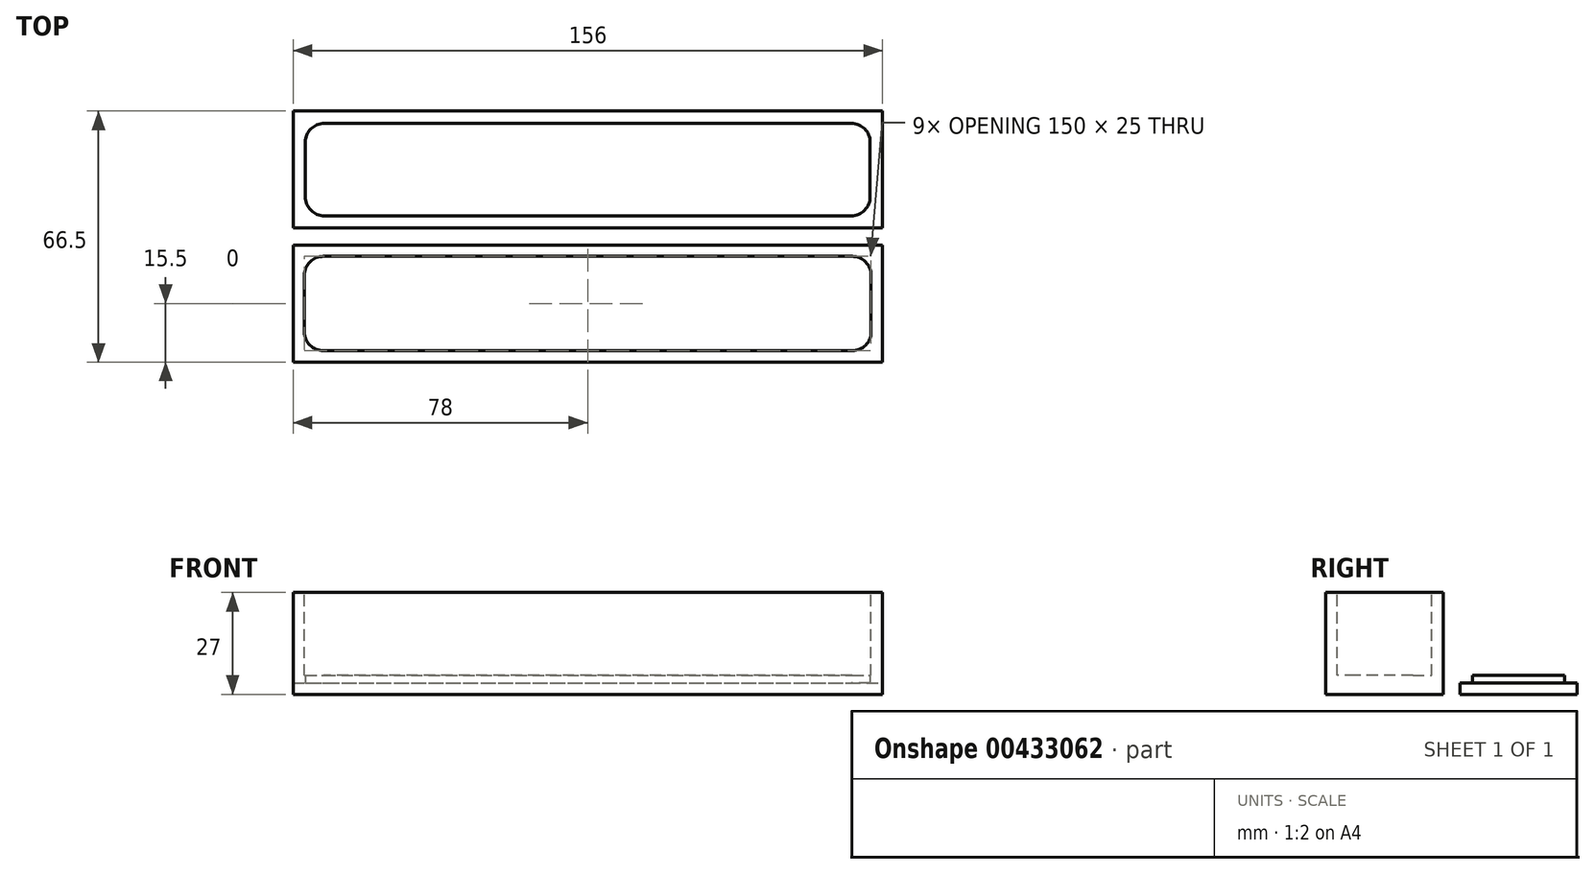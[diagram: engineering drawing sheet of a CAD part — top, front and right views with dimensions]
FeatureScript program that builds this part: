
annotation { "Feature Type Name" : "Feature", "Feature Type Description" : "" }
export const myFeature = defineFeature(function(context is Context, id is Id, definition is map)
    precondition{}
    {
        {
            var Q0;
            Q0=qCreatedBy(makeId("Top.planeOp"),FACE);
            var sketch = newSketch(context, id + "F0", { "sketchPlane" : qUnion([Q0])});
            skLineSegment(sketch, "E0.bottom", {"start": v(78, -15.5) * mm, "end": v(-78, -15.5) * mm});
            skLineSegment(sketch, "E0.top", {"start": v(78, 15.5) * mm, "end": v(-78, 15.5) * mm});
            skLineSegment(sketch, "E0.left", {"start": v(78, -15.5) * mm, "end": v(78, 15.5) * mm});
            skLineSegment(sketch, "E0.right", {"start": v(-78, -15.5) * mm, "end": v(-78, 15.5) * mm});
            skPoint(sketch, "E0.middle", {"position": v(0, 0) * mm});
            skSolve(sketch);
        }
        {
            var Q0;
            Q0 = qSketchRegion(id + "F0", true);
            extrude(context, id + "F1", {"entities" : qUnion([Q0]), "depth" : 27 * mm});
        }
        {
            var Q0;
            Q0=makeQuery(id+"F1.opExtrude","CAP_FACE",FACE,{"disambiguationData":[OSD([sQuery(id+"F0.wireOp",EDGE,"E0.bottom"),sQuery(id+"F0.wireOp",EDGE,"E0.top"),sQuery(id+"F0.wireOp",EDGE,"E0.left"),sQuery(id+"F0.wireOp",EDGE,"E0.right")])],"isStart":false});
            var sketch = newSketch(context, id + "F2", { "sketchPlane" : qUnion([Q0])});
            skLineSegment(sketch, "E1.bottom", {"start": v(70, 12.5) * mm, "end": v(-70, 12.5) * mm});
            skLineSegment(sketch, "E1.top", {"start": v(70, -12.5) * mm, "end": v(-70, -12.5) * mm});
            skLineSegment(sketch, "E1.left", {"start": v(75, 7.5) * mm, "end": v(75, -7.5) * mm});
            skLineSegment(sketch, "E1.right", {"start": v(-75, 7.5) * mm, "end": v(-75, -7.5) * mm});
            skPoint(sketch, "E1.middle", {"position": v(0, 0) * mm});
            skPoint(sketch, "E2.visualSharp", {"position": v(-75, 12.5) * mm});
            skArc(sketch, "E2.filletArc", {"start": v(-70, 12.5) * mm, "mid": v(-73.54, 11.04) * mm, "end": v(-75, 7.5) * mm});
            skPoint(sketch, "E3.visualSharp", {"position": v(-75, -12.5) * mm});
            skArc(sketch, "E3.filletArc", {"start": v(-75, -7.5) * mm, "mid": v(-73.54, -11.04) * mm, "end": v(-70, -12.5) * mm});
            skPoint(sketch, "E4.visualSharp", {"position": v(75, -12.5) * mm});
            skArc(sketch, "E4.filletArc", {"start": v(70, -12.5) * mm, "mid": v(73.54, -11.04) * mm, "end": v(75, -7.5) * mm});
            skPoint(sketch, "E5.visualSharp", {"position": v(75, 12.5) * mm});
            skArc(sketch, "E5.filletArc", {"start": v(75, 7.5) * mm, "mid": v(73.54, 11.04) * mm, "end": v(70, 12.5) * mm});
            skSolve(sketch);
        }
        {
            var Q0;
            Q0 = qSketchRegion(id + "F2", true);
            extrude(context, id + "F3", {"entities" : qUnion([Q0]), "operationType" : NewBodyOperationType.REMOVE, "oppositeDirection" : true, "depth" : 22 * mm});
        }
        {
            var Q0;
            Q0=qCreatedBy(makeId("Top.planeOp"),FACE);
            var sketch = newSketch(context, id + "F4", { "sketchPlane" : qUnion([Q0])});
            skLineSegment(sketch, "E6.bottom", {"start": v(-78, 20) * mm, "end": v(78, 20) * mm});
            skLineSegment(sketch, "E6.top", {"start": v(-78, 51) * mm, "end": v(78, 51) * mm});
            skLineSegment(sketch, "E6.left", {"start": v(-78, 20) * mm, "end": v(-78, 51) * mm});
            skLineSegment(sketch, "E6.right", {"start": v(78, 20) * mm, "end": v(78, 51) * mm});
            skSolve(sketch);
        }
        {
            var Q0;
            Q0 = qSketchRegion(id + "F4", true);
            extrude(context, id + "F5", {"entities" : qUnion([Q0]), "depth" : 3 * mm});
        }
        {
            var Q0;
            Q0=makeQuery(id+"F5.opExtrude","CAP_FACE",FACE,{"disambiguationData":[OSD([sQuery(id+"F4.wireOp",EDGE,"E6.bottom"),sQuery(id+"F4.wireOp",EDGE,"E6.top"),sQuery(id+"F4.wireOp",EDGE,"E6.left"),sQuery(id+"F4.wireOp",EDGE,"E6.right")])],"isStart":false});
            var sketch = newSketch(context, id + "F6", { "sketchPlane" : qUnion([Q0])});
            skLineSegment(sketch, "E7.bottom", {"start": v(-69.75, 23.25) * mm, "end": v(69.75, 23.25) * mm});
            skLineSegment(sketch, "E7.top", {"start": v(-69.75, 47.75) * mm, "end": v(69.75, 47.75) * mm});
            skLineSegment(sketch, "E7.left", {"start": v(-74.75, 28.25) * mm, "end": v(-74.75, 42.75) * mm});
            skLineSegment(sketch, "E7.right", {"start": v(74.75, 28.25) * mm, "end": v(74.75, 42.75) * mm});
            skPoint(sketch, "E8.visualSharp", {"position": v(-74.75, 47.75) * mm});
            skArc(sketch, "E8.filletArc", {"start": v(-69.75, 47.75) * mm, "mid": v(-73.29, 46.29) * mm, "end": v(-74.75, 42.75) * mm});
            skPoint(sketch, "E9.visualSharp", {"position": v(-74.75, 23.25) * mm});
            skArc(sketch, "E9.filletArc", {"start": v(-74.75, 28.25) * mm, "mid": v(-73.29, 24.71) * mm, "end": v(-69.75, 23.25) * mm});
            skPoint(sketch, "E10.visualSharp", {"position": v(74.75, 23.25) * mm});
            skArc(sketch, "E10.filletArc", {"start": v(69.75, 23.25) * mm, "mid": v(73.29, 24.71) * mm, "end": v(74.75, 28.25) * mm});
            skPoint(sketch, "E11.visualSharp", {"position": v(74.75, 47.75) * mm});
            skArc(sketch, "E11.filletArc", {"start": v(74.75, 42.75) * mm, "mid": v(73.29, 46.29) * mm, "end": v(69.75, 47.75) * mm});
            skSolve(sketch);
        }
        {
            var Q0;
            Q0 = qSketchRegion(id + "F6", true);
            extrude(context, id + "F7", {"entities" : qUnion([Q0]), "operationType" : NewBodyOperationType.ADD, "depth" : 2 * mm});
        }
    });
